# Revit family: Edelstahlrohrschelle V2A, M12, Ø103-168
name_source: partatom
category: HLS-Bauteile
revit_build: Autodesk Revit 2017 (Build: 20190507_1515(x64)
units: mm (PartAtom-declared; Revit-internal decimal feet)

## family parameters
Arbeitsebenenbasiert = Ja
Beim Laden mit Abzugskörper schneiden = Nein
Bemaßung runder Anschluss = Durchmesser verwenden
Gemeinsam genutzt = Ja
Immer vertikal = Nein
Raumberechnungspunkt = Nein
Teiletyp = Normal

## types (8) — shared parameters
A = 14 mm  [stored 0.0459318 ft]
Anschluss = M12
Anschlußhöhe = 14 mm
Bauart = zweiteilig
DF1 = 21 mm  [stored 0.0688976 ft]
DF2 = 27 mm  [stored 0.0885827 ft]
DVS = 9 mm  [stored 0.0295276 ft]
Fabrikat = MEFA
Firma = MEFA Befestigungs- und Montagesysteme GmbH
HGA = 11 mm  [stored 0.0360892 ft]
Kurztext1 = Rohrschelle Edelstahl V2A 25x3,0
MB = 25 mm  [stored 0.082021 ft]
MD = 3 mm  [stored 0.00984252 ft]
Material = Edelstahl
Materialmaße = 25x3,0 mm
Mengeneinheit = St
Verschluss = Schraubenverschluss
Verschluss-Schraube = M8
Vorgabe-Ansicht = 1219 mm
max. zul. Last horizontal = 0.00 kN
max. zul. Last vertikal = 0.00 kN
vpe = 50 St
zero-valued in all types: Nennweite DN Rohr, Rohraußendurchmesser, Stärke Material

## per-type parameters (varying)
| type | AB | Achsabstand | Artikelnummer | B | D | Dmax | Dmin | EAN | Gewicht | Gewicht pro Bauteil | H | Kurztext2 | R | RM | Rohraußendurchmesser Zoll | S | max. Rohraußendurchmesser | min. Rohraußendurchmesser |
| Edelstahlrohrschelle V2A, M12, Ø103-110 | 7 mm  [stored 0.0229659 ft] | 142 mm | 0461317 | 164 mm | 110 mm  [stored 0.360892 ft] | 110 mm  [stored 0.360892 ft] | 103 mm  [stored 0.337927 ft] | 4250928411426 | 0.30 kg | 0.30 kg | 127 mm  [stored 0.416667 ft] | 103 - 110 mm M12 | 55 mm  [stored 0.180446 ft] | 58 mm  [stored 0.190289 ft] | Zoll | 143 mm | 110 mm  [stored 0.360892 ft] | 103 mm  [stored 0.337927 ft] |
| Edelstahlrohrschelle V2A, M12, Ø112-117 | 5 mm  [stored 0.0164042 ft] | 150 mm | 0461318 | 171 mm | 117 mm  [stored 0.383858 ft] | 117 mm  [stored 0.383858 ft] | 112 mm  [stored 0.367454 ft] | 4250928411433 | 0.31 kg | 0.31 kg | 134 mm  [stored 0.439633 ft] | 112 - 117 mm M12 | 59 mm | 62 mm | 4 Zoll | 150 mm | 117 mm  [stored 0.383858 ft] | 112 mm  [stored 0.367454 ft] |
| Edelstahlrohrschelle V2A, M12, Ø118-126 | 8 mm  [stored 0.0262467 ft] | 158 mm | 0467319 | 180 mm | 126 mm  [stored 0.413386 ft] | 126 mm  [stored 0.413386 ft] | 118 mm | 4250928411761 | 0.32 kg | 0.32 kg | 143 mm | 118 - 126 mm M12 | 63 mm  [stored 0.206693 ft] | 66 mm  [stored 0.216535 ft] | Zoll | 159 mm | 126 mm  [stored 0.413386 ft] | 118 mm |
| Edelstahlrohrschelle V2A, M12, Ø129-137 | 8 mm  [stored 0.0262467 ft] | 169 mm | 0467320 | 191 mm | 137 mm  [stored 0.449475 ft] | 137 mm  [stored 0.449475 ft] | 129 mm  [stored 0.423228 ft] | 4250928411778 | 0.34 kg | 0.34 kg | 154 mm | 129 - 137 mm M12 | 69 mm | 72 mm | Zoll | 170 mm | 137 mm  [stored 0.449475 ft] | 129 mm  [stored 0.423228 ft] |
| Edelstahlrohrschelle V2A, M12, Ø138-142 | 4 mm  [stored 0.0131234 ft] | 176 mm | 0467321 | 196 mm | 142 mm  [stored 0.465879 ft] | 142 mm  [stored 0.465879 ft] | 138 mm  [stored 0.452756 ft] | 4250928411785 | 0.36 kg | 0.36 kg | 159 mm | 138 - 142 mm M12 | 71 mm  [stored 0.23294 ft] | 74 mm  [stored 0.242782 ft] | 5 Zoll | 175 mm | 142 mm  [stored 0.465879 ft] | 138 mm  [stored 0.452756 ft] |
| Edelstahlrohrschelle V2A, M12, Ø143-151 | 8 mm  [stored 0.0262467 ft] | 184 mm | 0467322 | 205 mm | 151 mm | 151 mm | 143 mm | 4250928411792 | 0.37 kg | 0.37 kg | 168 mm | 143 - 151 mm M12 | 76 mm | 79 mm | Zoll | 184 mm | 151 mm | 143 mm |
| Edelstahlrohrschelle V2A, M12, Ø152-159 | 7 mm  [stored 0.0229659 ft] | 192 mm | 0467323 | 213 mm | 159 mm | 159 mm | 152 mm | 4250928411808 | 0.38 kg | 0.38 kg | 176 mm | 152 - 159 mm M12 | 80 mm | 83 mm | Zoll | 192 mm | 159 mm | 152 mm |
| Edelstahlrohrschelle V2A, M12, Ø160-168 | 8 mm  [stored 0.0262467 ft] | 201 mm | 0467324 | 222 mm | 168 mm | 168 mm | 160 mm | 4250928411815 | 0.40 kg | 0.40 kg | 185 mm | 160 - 168 mm M12 | 84 mm  [stored 0.275591 ft] | 87 mm  [stored 0.285433 ft] | 6 Zoll | 201 mm | 168 mm | 160 mm |

note: [stored X ft] marks values corroborated as IEEE doubles in the binary element streams (Revit-internal decimal feet)

## geometry (parser evidence)
native form markers: Sweep x5
no freeform markers — native parametric forms only
